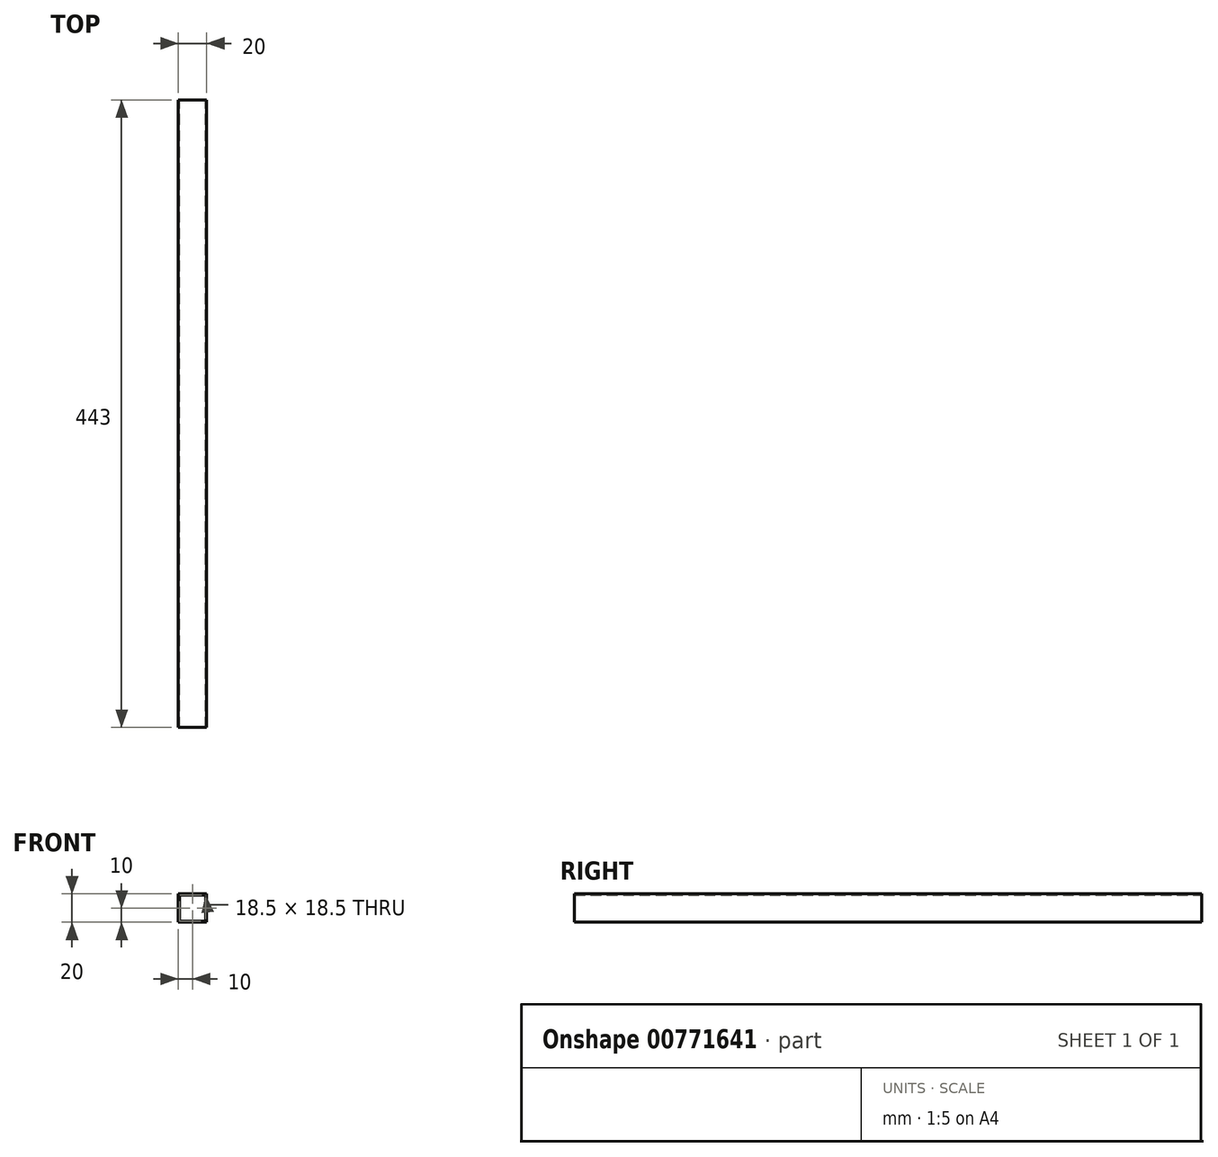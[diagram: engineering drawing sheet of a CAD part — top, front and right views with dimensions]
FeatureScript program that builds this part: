
annotation { "Feature Type Name" : "Feature", "Feature Type Description" : "" }
export const myFeature = defineFeature(function(context is Context, id is Id, definition is map)
    precondition{}
    {
        {
            var Q0;
            Q0=qCreatedBy(makeId("Front.planeOp"),FACE);
            var sketch = newSketch(context, id + "F0", { "sketchPlane" : qUnion([Q0])});
            skLineSegment(sketch, "E0.bottom", {"start": v(-10, 10) * mm, "end": v(10, 10) * mm});
            skLineSegment(sketch, "E0.top", {"start": v(-10, -10) * mm, "end": v(10, -10) * mm});
            skLineSegment(sketch, "E0.left", {"start": v(-10, 10) * mm, "end": v(-10, -10) * mm});
            skLineSegment(sketch, "E0.right", {"start": v(10, 10) * mm, "end": v(10, -10) * mm});
            skLineSegment(sketch, "E1.bottom", {"start": v(-9.25, 9.25) * mm, "end": v(9.25, 9.25) * mm});
            skLineSegment(sketch, "E1.top", {"start": v(-9.25, -9.25) * mm, "end": v(9.25, -9.25) * mm});
            skLineSegment(sketch, "E1.left", {"start": v(-9.25, 9.25) * mm, "end": v(-9.25, -9.25) * mm});
            skLineSegment(sketch, "E1.right", {"start": v(9.25, 9.25) * mm, "end": v(9.25, -9.25) * mm});
            skSolve(sketch);
        }
        {
            var Q0;
            Q0 = qSketchRegion(id + "F0", true);
            extrude(context, id + "F1", {"entities" : qUnion([Q0]), "depth" : 443 * mm, "offsetDistance" : 25 * mm});
        }
    });
